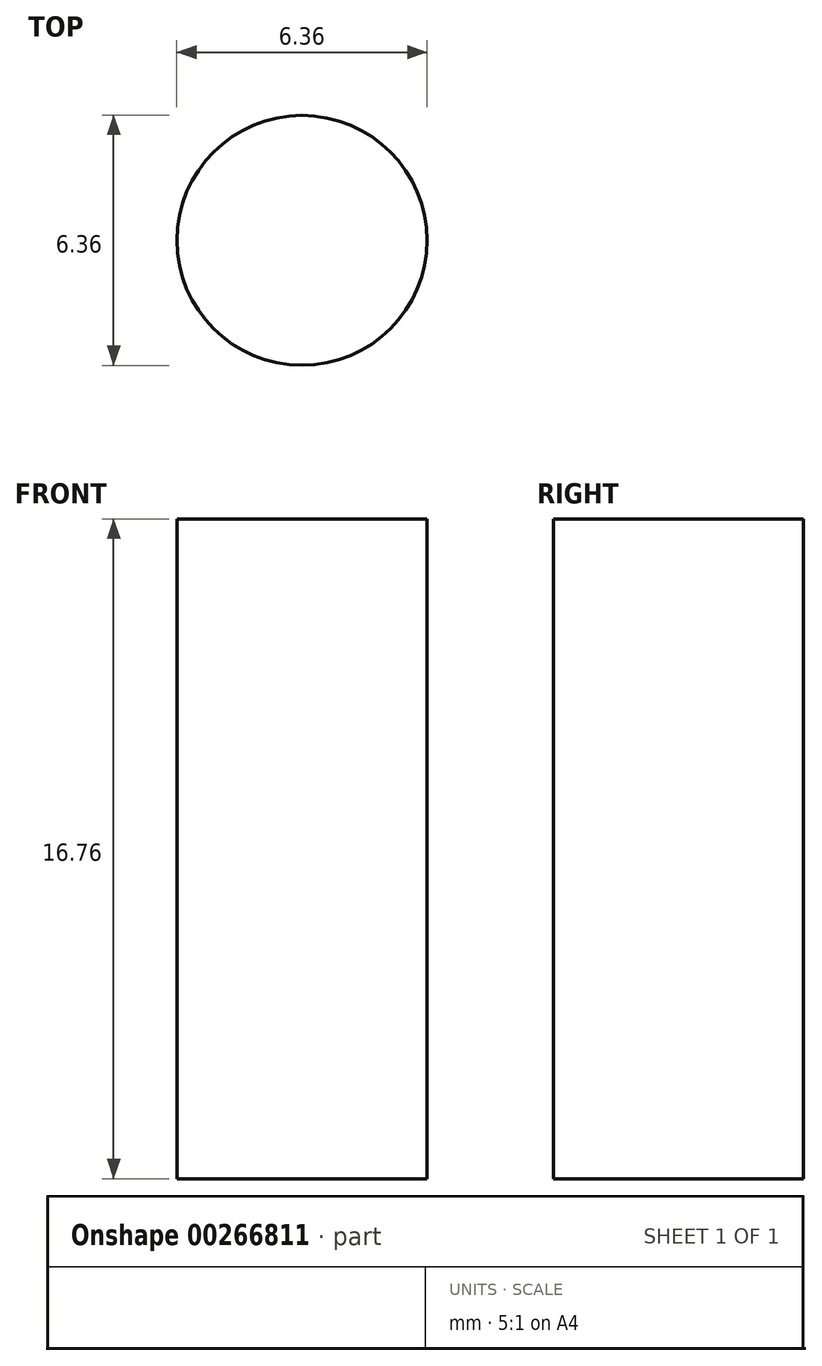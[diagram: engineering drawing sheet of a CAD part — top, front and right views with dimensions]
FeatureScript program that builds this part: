
annotation { "Feature Type Name" : "Feature", "Feature Type Description" : "" }
export const myFeature = defineFeature(function(context is Context, id is Id, definition is map)
    precondition{}
    {
        {
            var Q0;
            Q0=qCreatedBy(makeId("Top.planeOp"),FACE);
            var sketch = newSketch(context, id + "F0", { "sketchPlane" : qUnion([Q0])});
            skCircle(sketch, "E0", {"center": v(0, 0) * mm, "radius": 3.18 * mm});
            skSolve(sketch);
        }
        {
            var Q0;
            Q0=makeQuery(id+"F0.imprint","IMPRINT",FACE,{"disambiguationData":[TD([[makeQuery(id+"F0.imprint","IMPRINT",EDGE,{"derivedFrom":sQuery(id+"F0.wireOp",EDGE,"E0")}),1.0]])]});
            extrude(context, id + "F1", {"entities" : qUnion([Q0]), "depth" : 16.76 * mm});
        }
    });
